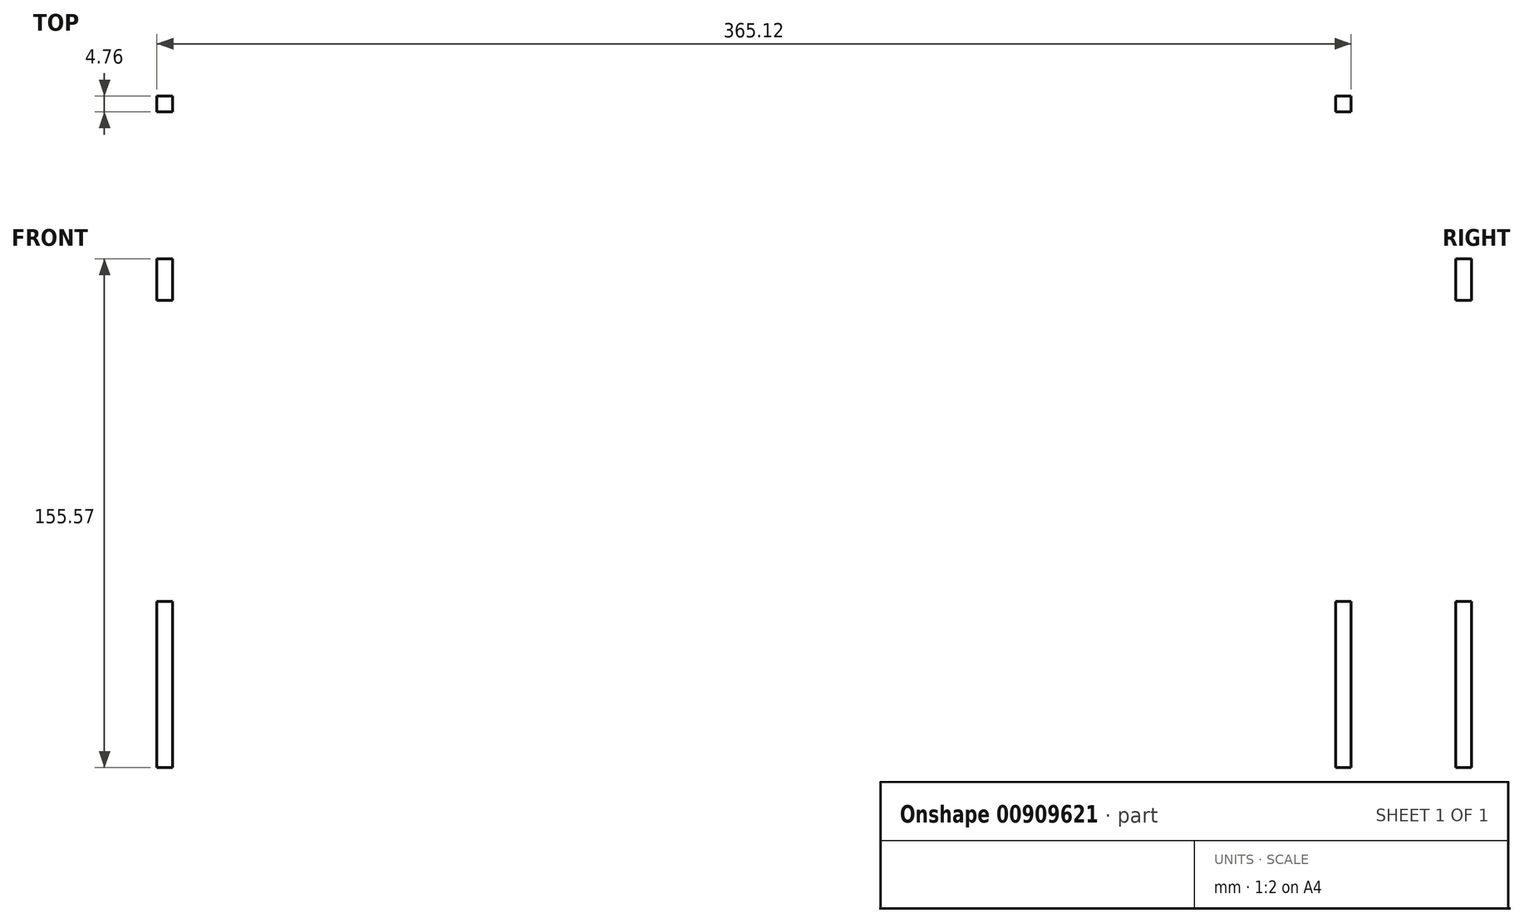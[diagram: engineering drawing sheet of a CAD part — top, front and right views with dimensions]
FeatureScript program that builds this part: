
annotation { "Feature Type Name" : "Feature", "Feature Type Description" : "" }
export const myFeature = defineFeature(function(context is Context, id is Id, definition is map)
    precondition{}
    {
        {
            var Q0;
            Q0=qCreatedBy(makeId("Front.planeOp"),FACE);
            var sketch = newSketch(context, id + "F0", { "sketchPlane" : qUnion([Q0])});
            skLineSegment(sketch, "E0.bottom", {"start": v(-182.56, 88.9) * mm, "end": v(182.56, 88.9) * mm});
            skLineSegment(sketch, "E0.top", {"start": v(-182.56, -88.9) * mm, "end": v(182.56, -88.9) * mm});
            skLineSegment(sketch, "E0.left", {"start": v(-182.56, 88.9) * mm, "end": v(-182.56, -88.9) * mm});
            skLineSegment(sketch, "E0.right", {"start": v(182.56, 88.9) * mm, "end": v(182.56, -88.9) * mm});
            skPoint(sketch, "E0.middle", {"position": v(0, 0) * mm});
            skLineSegment(sketch, "E1.0", {"start": v(-177.8, 88.9) * mm, "end": v(-177.8, -88.9) * mm});
            skLineSegment(sketch, "E2.0", {"start": v(177.8, 88.9) * mm, "end": v(177.8, -88.9) * mm});
            skLineSegment(sketch, "E3.bottom", {"start": v(-127, 31.75) * mm, "end": v(-76.2, 31.75) * mm});
            skLineSegment(sketch, "E3.top", {"start": v(-127, 25.4) * mm, "end": v(-76.2, 25.4) * mm});
            skLineSegment(sketch, "E3.left", {"start": v(-127, 31.75) * mm, "end": v(-127, 25.4) * mm});
            skLineSegment(sketch, "E3.right", {"start": v(-76.2, 31.75) * mm, "end": v(-76.2, 25.4) * mm});
            skLineSegment(sketch, "E4.0", {"start": v(-127.13, 31.88) * mm, "end": v(-76.07, 31.88) * mm});
            skLineSegment(sketch, "E4.1", {"start": v(-127.13, 31.88) * mm, "end": v(-127.13, 25.27) * mm});
            skLineSegment(sketch, "E4.2", {"start": v(-127.13, 25.27) * mm, "end": v(-76.07, 25.27) * mm});
            skLineSegment(sketch, "E4.3", {"start": v(-76.07, 31.88) * mm, "end": v(-76.07, 25.27) * mm});
            skLineSegment(sketch, "E5.1.0.0", {"start": v(-25.53, 31.88) * mm, "end": v(-25.53, 25.27) * mm});
            skLineSegment(sketch, "E5.1.0.1", {"start": v(-25.53, 31.88) * mm, "end": v(25.53, 31.88) * mm});
            skLineSegment(sketch, "E5.1.0.2", {"start": v(-25.53, 25.27) * mm, "end": v(25.53, 25.27) * mm});
            skLineSegment(sketch, "E5.1.0.3", {"start": v(25.4, 31.75) * mm, "end": v(25.4, 25.4) * mm});
            skLineSegment(sketch, "E5.1.0.4", {"start": v(-25.4, 31.75) * mm, "end": v(25.4, 31.75) * mm});
            skLineSegment(sketch, "E5.1.0.5", {"start": v(25.53, 31.88) * mm, "end": v(25.53, 25.27) * mm});
            skLineSegment(sketch, "E5.1.0.6", {"start": v(-25.4, 31.75) * mm, "end": v(-25.4, 25.4) * mm});
            skLineSegment(sketch, "E5.1.0.7", {"start": v(-25.4, 25.4) * mm, "end": v(25.4, 25.4) * mm});
            skLineSegment(sketch, "E5.2.0.0", {"start": v(76.07, 31.88) * mm, "end": v(76.07, 25.27) * mm});
            skLineSegment(sketch, "E5.2.0.1", {"start": v(76.07, 31.88) * mm, "end": v(127.13, 31.88) * mm});
            skLineSegment(sketch, "E5.2.0.2", {"start": v(76.07, 25.27) * mm, "end": v(127.13, 25.27) * mm});
            skLineSegment(sketch, "E5.2.0.3", {"start": v(127, 31.75) * mm, "end": v(127, 25.4) * mm});
            skLineSegment(sketch, "E5.2.0.4", {"start": v(76.2, 31.75) * mm, "end": v(127, 31.75) * mm});
            skLineSegment(sketch, "E5.2.0.5", {"start": v(127.13, 31.88) * mm, "end": v(127.13, 25.27) * mm});
            skLineSegment(sketch, "E5.2.0.6", {"start": v(76.2, 31.75) * mm, "end": v(76.2, 25.4) * mm});
            skLineSegment(sketch, "E5.2.0.7", {"start": v(76.2, 25.4) * mm, "end": v(127, 25.4) * mm});
            skLineSegment(sketch, "E5.direction1", {"start": v(-127, 25.4) * mm, "end": v(-25.4, 25.4) * mm, "construction": true});
            skLineSegment(sketch, "E6.bottom", {"start": v(-182.56, -88.9) * mm, "end": v(-177.8, -88.9) * mm});
            skLineSegment(sketch, "E6.top", {"start": v(-182.56, -38.1) * mm, "end": v(-177.8, -38.1) * mm});
            skLineSegment(sketch, "E6.left", {"start": v(-182.56, -88.9) * mm, "end": v(-182.56, -38.1) * mm});
            skLineSegment(sketch, "E6.right", {"start": v(-177.8, -88.9) * mm, "end": v(-177.8, -38.1) * mm});
            skLineSegment(sketch, "E7", {"start": v(0, 88.9) * mm, "end": v(0, -88.9) * mm, "construction": true});
            skLineSegment(sketch, "E8.MirrorCS", {"start": v(182.56, -88.9) * mm, "end": v(177.8, -88.9) * mm});
            skLineSegment(sketch, "E9.MirrorCS", {"start": v(182.56, -38.1) * mm, "end": v(177.8, -38.1) * mm});
            skLineSegment(sketch, "E10.MirrorCS", {"start": v(182.56, -88.9) * mm, "end": v(182.56, -38.1) * mm});
            skLineSegment(sketch, "E11.MirrorCS", {"start": v(177.8, -88.9) * mm, "end": v(177.8, -38.1) * mm});
            skLineSegment(sketch, "E12.bottom", {"start": v(-127, 88.9) * mm, "end": v(-76.2, 88.9) * mm});
            skLineSegment(sketch, "E12.top", {"start": v(-127, 93.66) * mm, "end": v(-76.2, 93.66) * mm});
            skLineSegment(sketch, "E12.left", {"start": v(-127, 88.9) * mm, "end": v(-127, 93.66) * mm});
            skLineSegment(sketch, "E12.right", {"start": v(-76.2, 88.9) * mm, "end": v(-76.2, 93.66) * mm});
            skLineSegment(sketch, "E13.1.0.0", {"start": v(-25.4, 88.9) * mm, "end": v(25.4, 88.9) * mm});
            skLineSegment(sketch, "E13.1.0.1", {"start": v(25.4, 88.9) * mm, "end": v(25.4, 93.66) * mm});
            skLineSegment(sketch, "E13.1.0.2", {"start": v(-25.4, 93.66) * mm, "end": v(25.4, 93.66) * mm});
            skLineSegment(sketch, "E13.1.0.3", {"start": v(-25.4, 88.9) * mm, "end": v(-25.4, 93.66) * mm});
            skLineSegment(sketch, "E13.2.0.0", {"start": v(76.2, 88.9) * mm, "end": v(127, 88.9) * mm});
            skLineSegment(sketch, "E13.2.0.1", {"start": v(127, 88.9) * mm, "end": v(127, 93.66) * mm});
            skLineSegment(sketch, "E13.2.0.2", {"start": v(76.2, 93.66) * mm, "end": v(127, 93.66) * mm});
            skLineSegment(sketch, "E13.2.0.3", {"start": v(76.2, 88.9) * mm, "end": v(76.2, 93.66) * mm});
            skLineSegment(sketch, "E13.direction1", {"start": v(-127, 88.9) * mm, "end": v(-25.4, 88.9) * mm, "construction": true});
            skLineSegment(sketch, "E14.bottom", {"start": v(-177.8, 46.3) * mm, "end": v(-158.75, 46.3) * mm});
            skLineSegment(sketch, "E14.top", {"start": v(-177.8, 42.6) * mm, "end": v(-158.75, 42.6) * mm});
            skLineSegment(sketch, "E14.left", {"start": v(-177.8, 46.3) * mm, "end": v(-177.8, 42.6) * mm});
            skLineSegment(sketch, "E14.right", {"start": v(-158.75, 46.3) * mm, "end": v(-158.75, 42.6) * mm});
            skPoint(sketch, "E15", {"position": v(-177.8, 44.45) * mm});
            skLineSegment(sketch, "E16.bottom", {"start": v(-169.86, 48.58) * mm, "end": v(-166.69, 48.58) * mm});
            skLineSegment(sketch, "E16.top", {"start": v(-169.86, 40.32) * mm, "end": v(-166.69, 40.32) * mm});
            skLineSegment(sketch, "E16.left", {"start": v(-169.86, 48.58) * mm, "end": v(-169.86, 40.32) * mm});
            skLineSegment(sketch, "E16.right", {"start": v(-166.69, 48.58) * mm, "end": v(-166.69, 40.32) * mm});
            skPoint(sketch, "E17", {"position": v(-166.69, 44.45) * mm});
            skLineSegment(sketch, "E18", {"start": v(-177.8, 44.45) * mm, "end": v(-158.75, 44.45) * mm, "construction": true});
            skLineSegment(sketch, "E19", {"start": v(-168.28, 48.58) * mm, "end": v(-168.28, 40.32) * mm, "construction": true});
            skLineSegment(sketch, "E20.bottom", {"start": v(-177.8, 66.68) * mm, "end": v(-182.56, 66.68) * mm});
            skLineSegment(sketch, "E20.top", {"start": v(-177.8, 53.98) * mm, "end": v(-182.56, 53.98) * mm});
            skLineSegment(sketch, "E20.left", {"start": v(-177.8, 66.68) * mm, "end": v(-177.8, 53.98) * mm});
            skLineSegment(sketch, "E20.right", {"start": v(-182.56, 66.68) * mm, "end": v(-182.56, 53.98) * mm});
            skPoint(sketch, "E21", {"position": v(-177.8, 60.33) * mm});
            skPoint(sketch, "E22.MirrorP", {"position": v(-177.8, 28.58) * mm});
            skLineSegment(sketch, "E23.MirrorCS", {"start": v(-182.56, 22.23) * mm, "end": v(-182.56, 34.93) * mm});
            skLineSegment(sketch, "E24.MirrorCS", {"start": v(-177.8, 22.23) * mm, "end": v(-182.56, 22.23) * mm});
            skLineSegment(sketch, "E25.MirrorCS", {"start": v(-177.8, 34.93) * mm, "end": v(-182.56, 34.93) * mm});
            skLineSegment(sketch, "E26.MirrorCS", {"start": v(-177.8, 22.23) * mm, "end": v(-177.8, 34.93) * mm});
            skLineSegment(sketch, "E27.MirrorCS", {"start": v(177.8, 46.3) * mm, "end": v(177.8, 42.6) * mm});
            skPoint(sketch, "E28.MirrorP", {"position": v(177.8, 60.33) * mm});
            skLineSegment(sketch, "E29.MirrorCS", {"start": v(182.56, 66.68) * mm, "end": v(182.56, 53.98) * mm});
            skLineSegment(sketch, "E30.MirrorCS", {"start": v(177.8, 66.68) * mm, "end": v(182.56, 66.68) * mm});
            skPoint(sketch, "E31.MirrorP", {"position": v(177.8, 28.58) * mm});
            skLineSegment(sketch, "E32.MirrorCS", {"start": v(182.56, 22.23) * mm, "end": v(182.56, 34.93) * mm});
            skLineSegment(sketch, "E33.MirrorCS", {"start": v(177.8, 34.93) * mm, "end": v(182.56, 34.93) * mm});
            skLineSegment(sketch, "E34.MirrorCS", {"start": v(177.8, 53.98) * mm, "end": v(182.56, 53.98) * mm});
            skPoint(sketch, "E35.MirrorP", {"position": v(177.8, 44.45) * mm});
            skLineSegment(sketch, "E36.MirrorCS", {"start": v(177.8, 22.23) * mm, "end": v(177.8, 34.93) * mm});
            skLineSegment(sketch, "E37.MirrorCS", {"start": v(177.8, 66.68) * mm, "end": v(177.8, 53.98) * mm});
            skLineSegment(sketch, "E38.MirrorCS", {"start": v(177.8, 22.23) * mm, "end": v(182.56, 22.23) * mm});
            skLineSegment(sketch, "E39.MirrorCS", {"start": v(158.75, 46.3) * mm, "end": v(158.75, 42.6) * mm});
            skLineSegment(sketch, "E40.MirrorCS", {"start": v(169.86, 40.32) * mm, "end": v(166.69, 40.32) * mm});
            skLineSegment(sketch, "E41.MirrorCS", {"start": v(169.86, 48.58) * mm, "end": v(166.69, 48.58) * mm});
            skLineSegment(sketch, "E42.MirrorCS", {"start": v(168.27, 48.58) * mm, "end": v(168.27, 40.32) * mm, "construction": true});
            skLineSegment(sketch, "E43.MirrorCS", {"start": v(166.69, 48.58) * mm, "end": v(166.69, 40.32) * mm});
            skLineSegment(sketch, "E44.MirrorCS", {"start": v(177.8, 44.45) * mm, "end": v(158.75, 44.45) * mm, "construction": true});
            skLineSegment(sketch, "E45.MirrorCS", {"start": v(177.8, 46.3) * mm, "end": v(158.75, 46.3) * mm});
            skLineSegment(sketch, "E46.MirrorCS", {"start": v(169.86, 48.58) * mm, "end": v(169.86, 40.32) * mm});
            skPoint(sketch, "E47.MirrorP", {"position": v(166.69, 44.45) * mm});
            skLineSegment(sketch, "E48.MirrorCS", {"start": v(177.8, 42.6) * mm, "end": v(158.75, 42.6) * mm});
            skLineSegment(sketch, "E49.bottom", {"start": v(-52.64, 88.9) * mm, "end": v(-48.96, 88.9) * mm});
            skLineSegment(sketch, "E49.top", {"start": v(-52.64, 69.85) * mm, "end": v(-48.96, 69.85) * mm});
            skLineSegment(sketch, "E49.left", {"start": v(-52.64, 88.9) * mm, "end": v(-52.64, 69.85) * mm});
            skLineSegment(sketch, "E49.right", {"start": v(-48.96, 88.9) * mm, "end": v(-48.96, 69.85) * mm});
            skLineSegment(sketch, "E50", {"start": v(-50.8, 88.9) * mm, "end": v(-50.8, 69.85) * mm, "construction": true});
            skPoint(sketch, "E51", {"position": v(-50.8, 88.9) * mm});
            skLineSegment(sketch, "E52.bottom", {"start": v(-54.93, 79.38) * mm, "end": v(-46.67, 79.38) * mm});
            skLineSegment(sketch, "E52.top", {"start": v(-54.93, 76.2) * mm, "end": v(-46.67, 76.2) * mm});
            skLineSegment(sketch, "E52.left", {"start": v(-54.93, 79.38) * mm, "end": v(-54.93, 76.2) * mm});
            skLineSegment(sketch, "E52.right", {"start": v(-46.67, 79.37) * mm, "end": v(-46.67, 76.2) * mm});
            skLineSegment(sketch, "E53", {"start": v(-54.93, 77.79) * mm, "end": v(-46.67, 77.79) * mm, "construction": true});
            skPoint(sketch, "E54", {"position": v(-50.8, 76.2) * mm});
            skLineSegment(sketch, "E55.MirrorCS", {"start": v(52.64, 88.9) * mm, "end": v(48.96, 88.9) * mm});
            skLineSegment(sketch, "E56.MirrorCS", {"start": v(54.93, 79.37) * mm, "end": v(54.93, 76.2) * mm});
            skLineSegment(sketch, "E57.MirrorCS", {"start": v(46.67, 79.37) * mm, "end": v(46.67, 76.2) * mm});
            skLineSegment(sketch, "E58.MirrorCS", {"start": v(52.64, 69.85) * mm, "end": v(48.96, 69.85) * mm});
            skLineSegment(sketch, "E59.MirrorCS", {"start": v(54.93, 77.79) * mm, "end": v(46.67, 77.79) * mm, "construction": true});
            skLineSegment(sketch, "E60.MirrorCS", {"start": v(54.93, 76.2) * mm, "end": v(46.67, 76.2) * mm});
            skPoint(sketch, "E61.MirrorP", {"position": v(50.8, 88.9) * mm});
            skLineSegment(sketch, "E62.MirrorCS", {"start": v(48.96, 88.9) * mm, "end": v(48.96, 69.85) * mm});
            skLineSegment(sketch, "E63.MirrorCS", {"start": v(54.93, 79.38) * mm, "end": v(46.67, 79.38) * mm});
            skLineSegment(sketch, "E64.MirrorCS", {"start": v(50.8, 88.9) * mm, "end": v(50.8, 69.85) * mm, "construction": true});
            skPoint(sketch, "E65.MirrorP", {"position": v(50.8, 76.2) * mm});
            skLineSegment(sketch, "E66.MirrorCS", {"start": v(52.64, 88.9) * mm, "end": v(52.64, 69.85) * mm});
            skCircle(sketch, "E67", {"center": v(75.07, -46.92) * mm, "radius": 1.59 * mm});
            skCircle(sketch, "E68", {"center": v(75.07, -71.92) * mm, "radius": 1.59 * mm});
            skCircle(sketch, "E69", {"center": v(-74.93, -46.92) * mm, "radius": 1.59 * mm});
            skCircle(sketch, "E70", {"center": v(-74.93, -71.92) * mm, "radius": 1.59 * mm});
            skSolve(sketch);
        }
        {
            var Q0;
            Q0=makeQuery(id+"F0.imprint","IMPRINT",FACE,{"disambiguationData":[TD([[makeQuery(id+"F0.imprint","IMPRINT",EDGE,{"derivedFrom":sQuery(id+"F0.wireOp",EDGE,"E0.top")}),1.0]])]});
            var Q1;
            Q1=makeQuery(id+"F0.imprint","IMPRINT",FACE,{"disambiguationData":[TD([[makeQuery(id+"F0.imprint","IMPRINT",EDGE,{"derivedFrom":sQuery(id+"F0.wireOp",EDGE,"E8.MirrorCS")}),-1.0]])]});
            var Q2;
            Q2=makeQuery(id+"F0.imprint","IMPRINT",FACE,{"disambiguationData":[TD([[makeQuery(id+"F0.imprint","IMPRINT",EDGE,{"derivedFrom":sQuery(id+"F0.wireOp",EDGE,"E6.bottom")}),1.0]])]});
            var Q3;
            Q3=makeQuery(id+"F0.imprint","IMPRINT",FACE,{"disambiguationData":[TD([[makeQuery(id+"F0.imprint","IMPRINT",EDGE,{"derivedFrom":sQuery(id+"F0.wireOp",EDGE,"E12.bottom")}),1.0]])]});
            var Q4;
            Q4=makeQuery(id+"F0.imprint","IMPRINT",FACE,{"disambiguationData":[TD([[makeQuery(id+"F0.imprint","IMPRINT",EDGE,{"derivedFrom":sQuery(id+"F0.wireOp",EDGE,"E13.1.0.0")}),1.0]])]});
            var Q5;
            Q5=makeQuery(id+"F0.imprint","IMPRINT",FACE,{"disambiguationData":[TD([[makeQuery(id+"F0.imprint","IMPRINT",EDGE,{"derivedFrom":sQuery(id+"F0.wireOp",EDGE,"E13.2.0.0")}),1.0]])]});
            var Q6;
            Q6=makeQuery(id+"F0.imprint","IMPRINT",FACE,{"disambiguationData":[TD([[makeQuery(id+"F0.imprint","IMPRINT",EDGE,{"derivedFrom":sQuery(id+"F0.wireOp",EDGE,"E20.bottom")}),1.0]])]});
            var Q7;
            Q7=makeQuery(id+"F0.imprint","IMPRINT",FACE,{"disambiguationData":[TD([[makeQuery(id+"F0.imprint","IMPRINT",EDGE,{"derivedFrom":sQuery(id+"F0.wireOp",EDGE,"E23.MirrorCS")}),-1.0]])]});
            extrude(context, id + "F1", {"entities" : qUnion([Q0, Q1, Q2, Q3, Q4, Q5, Q6, Q7]), "depth" : 4.76 * mm, "offsetDistance" : 25.4 * mm});
        }
    });
